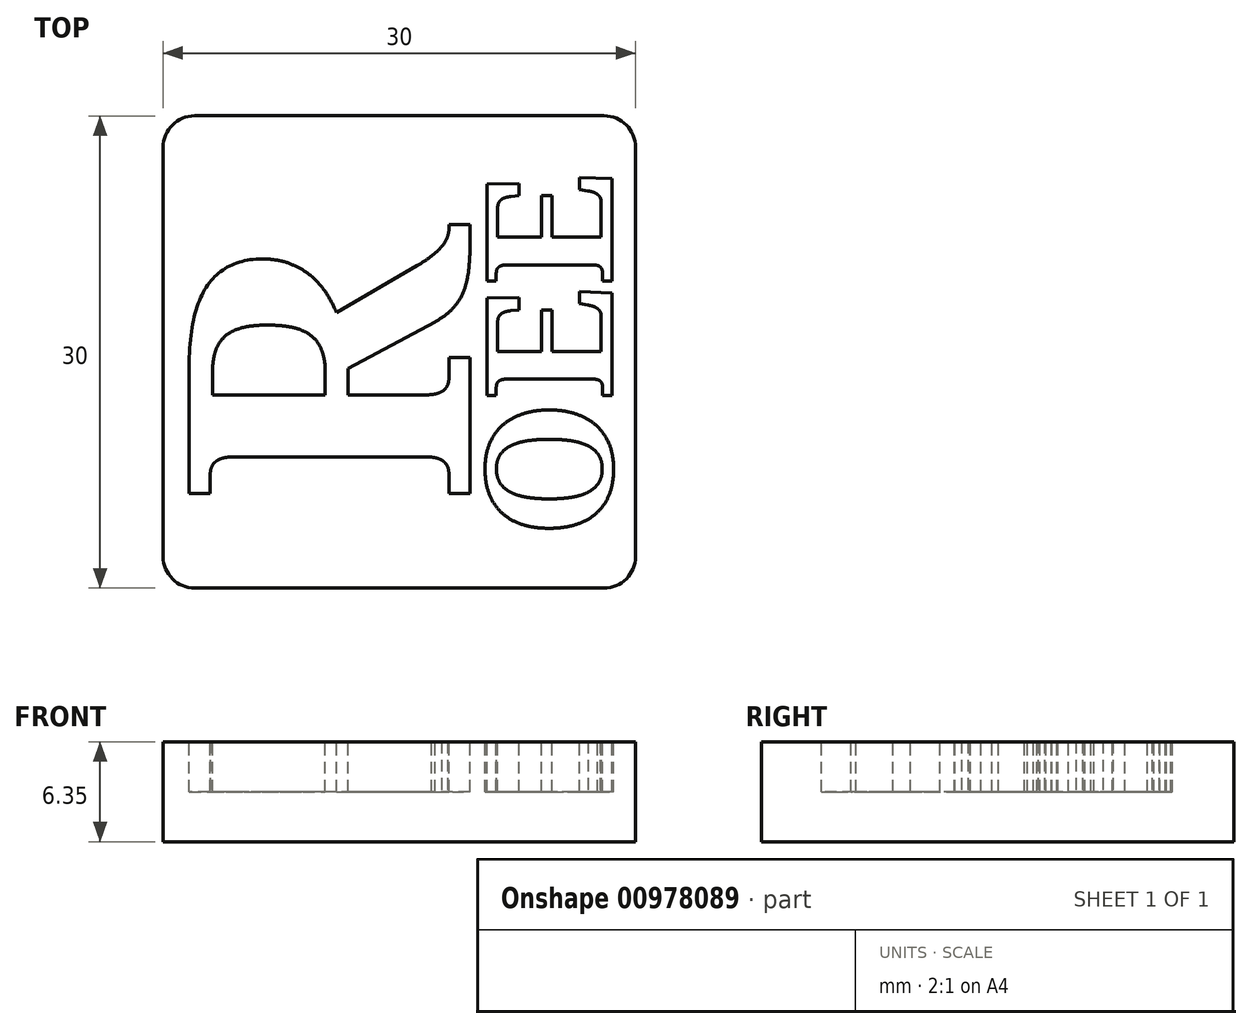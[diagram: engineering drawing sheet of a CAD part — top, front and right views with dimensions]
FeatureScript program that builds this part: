
annotation { "Feature Type Name" : "Feature", "Feature Type Description" : "" }
export const myFeature = defineFeature(function(context is Context, id is Id, definition is map)
    precondition{}
    {
        {
            var Q0;
            Q0=qCreatedBy(makeId("Top.planeOp"),FACE);
            var sketch = newSketch(context, id + "F0", { "sketchPlane" : qUnion([Q0])});
            skLineSegment(sketch, "E0.bottom", {"start": v(-15.27, 9.73) * mm, "end": v(10.73, 9.73) * mm});
            skLineSegment(sketch, "E0.top", {"start": v(-15.27, -20.27) * mm, "end": v(10.73, -20.27) * mm});
            skLineSegment(sketch, "E0.left", {"start": v(-17.27, 7.73) * mm, "end": v(-17.27, -18.27) * mm});
            skLineSegment(sketch, "E0.right", {"start": v(12.73, 7.73) * mm, "end": v(12.73, -18.27) * mm});
            skPoint(sketch, "E1.visualSharp", {"position": v(-17.27, 9.73) * mm});
            skArc(sketch, "E1.filletArc", {"start": v(-15.27, 9.73) * mm, "mid": v(-16.68, 9.15) * mm, "end": v(-17.27, 7.73) * mm});
            skPoint(sketch, "E2.visualSharp", {"position": v(12.73, 9.73) * mm});
            skArc(sketch, "E2.filletArc", {"start": v(12.73, 7.73) * mm, "mid": v(12.14, 9.15) * mm, "end": v(10.73, 9.73) * mm});
            skPoint(sketch, "E3.visualSharp", {"position": v(12.73, -20.27) * mm});
            skArc(sketch, "E3.filletArc", {"start": v(10.73, -20.27) * mm, "mid": v(12.14, -19.68) * mm, "end": v(12.73, -18.27) * mm});
            skPoint(sketch, "E4.visualSharp", {"position": v(-17.27, -20.27) * mm});
            skArc(sketch, "E4.filletArc", {"start": v(-17.27, -18.27) * mm, "mid": v(-16.68, -19.68) * mm, "end": v(-15.27, -20.27) * mm});
            skSolve(sketch);
        }
        {
            var Q0;
            Q0=qSketchRegion(id+"F0",true);
            extrude(context, id + "F1", {"entities" : qUnion([Q0]), "depth" : 6.35 * mm, "offsetDistance" : 25.4 * mm});
        }
        {
            var Q0;
            Q0=makeQuery(id+"F1.opExtrude","CAP_FACE",FACE,{"disambiguationData":[OSD([sQuery(id+"F0.wireOp",EDGE,"E0.bottom"),sQuery(id+"F0.wireOp",EDGE,"E0.top"),sQuery(id+"F0.wireOp",EDGE,"E0.left"),sQuery(id+"F0.wireOp",EDGE,"E0.right")])],"isStart":false});
            var sketch = newSketch(context, id + "F2", { "sketchPlane" : qUnion([Q0])});
            skText(sketch, "E5", { "text": "R", "fontName": "NotoSerif-Bold.ttf"});
            skText(sketch, "E6", { "text": "OEE", "fontName": "NotoSerif-Bold.ttf"});
            skPoint(sketch, "E7", {"position": v(-17.27, -5.27) * mm});
            skPoint(sketch, "E8", {"position": v(12.73, -5.27) * mm});
            const initialGuessF2  = {"E5": [0.00223, -0.01496, 0, 1, 0.018], "E6": [0.01123, -0.01708, 0, 1, 0.008]};
            skSetInitialGuess(sketch, initialGuessF2);
            skSolve(sketch);
        }
        {
            var Q0;
            Q0=qSketchRegion(id+"F2",true);
            extrude(context, id + "F3", {"entities" : qUnion([Q0]), "operationType" : NewBodyOperationType.REMOVE, "oppositeDirection" : true, "depth" : 3.17 * mm, "offsetDistance" : 25.4 * mm});
        }
    });
